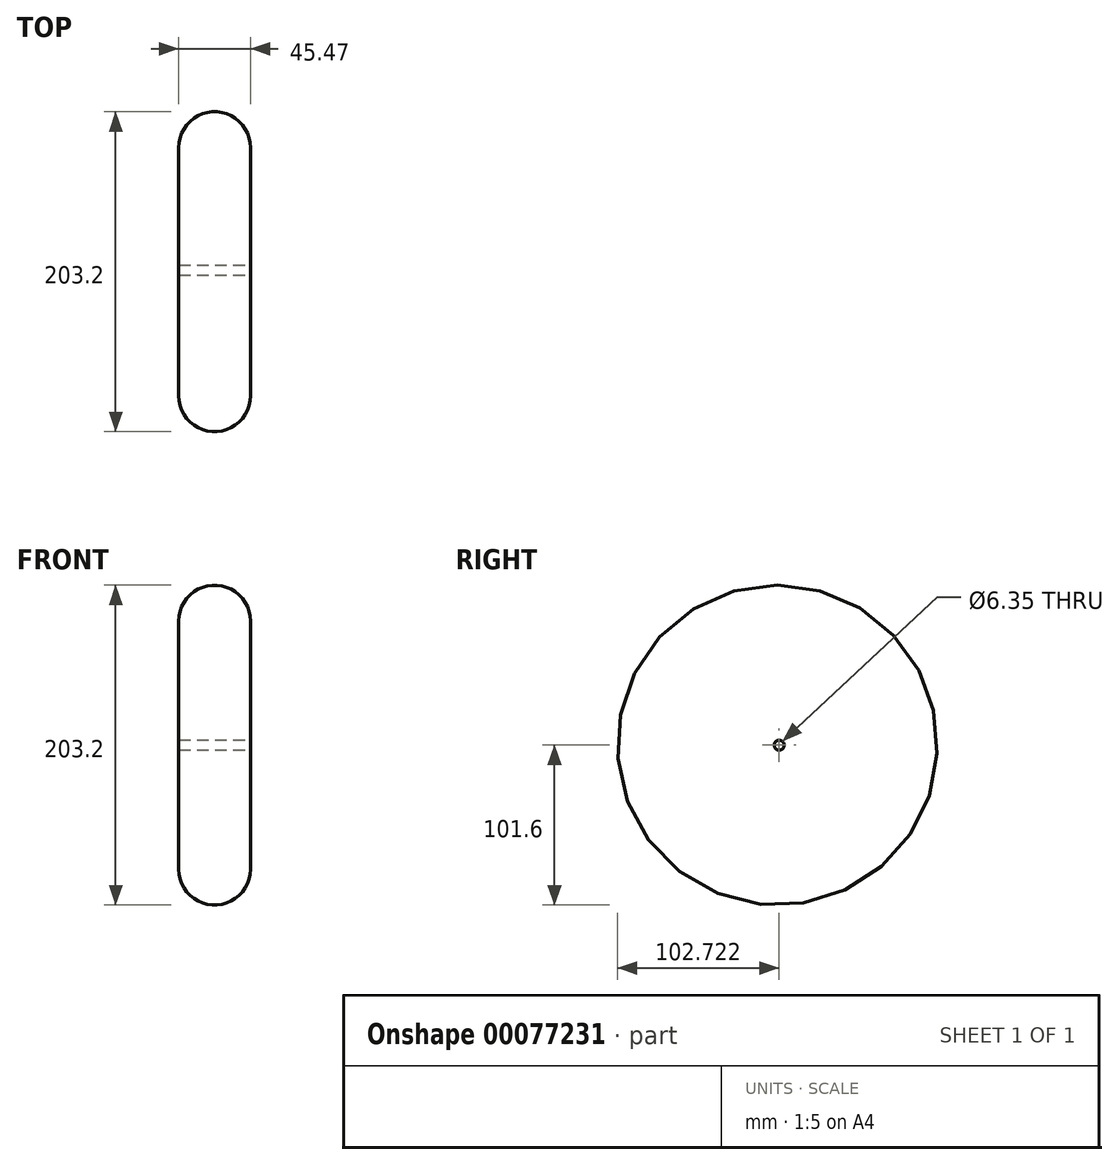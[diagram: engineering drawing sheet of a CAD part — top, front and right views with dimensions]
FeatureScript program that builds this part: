
annotation { "Feature Type Name" : "Feature", "Feature Type Description" : "" }
export const myFeature = defineFeature(function(context is Context, id is Id, definition is map)
    precondition{}
    {
        {
            var Q0;
            Q0=qCreatedBy(makeId("Front.planeOp"),FACE);
            var sketch = newSketch(context, id + "F0", { "sketchPlane" : qUnion([Q0])});
            skLineSegment(sketch, "E0", {"start": v(0, 78.87) * mm, "end": v(0, 0) * mm});
            skLineSegment(sketch, "E1", {"start": v(0, 0) * mm, "end": v(45.47, 0) * mm});
            skLineSegment(sketch, "E2", {"start": v(45.47, 0) * mm, "end": v(45.47, 78.87) * mm});
            skArc(sketch, "E3", {"start": v(45.47, 78.87) * mm, "mid": v(22.73, 101.6) * mm, "end": v(0, 78.87) * mm});
            skPoint(sketch, "E4", {"position": v(22.73, 101.6) * mm});
            skPoint(sketch, "E4.positionSnap0", {"position": v(22.73, 101.6) * mm});
            skSolve(sketch);
        }
        {
            var Q0;
            Q0=makeQuery(id+"F0.imprint","IMPRINT",FACE,{"disambiguationData":[TD([[makeQuery(id+"F0.imprint","IMPRINT",EDGE,{"derivedFrom":sQuery(id+"F0.wireOp",EDGE,"E0")}),1.0]])]});
            var Q1;
            Q1=sQuery(id+"F0.wireOp",EDGE,"E1");
            revolve(context, id + "F1", {"entities" : qUnion([Q0]), "axis" : qUnion([Q1]), "revolveType" : RevolveType.FULL});
        }
        {
            var Q0;
            Q0=makeQuery(id+"F1.opRevolve","SWEPT_FACE",FACE,{"disambiguationData":[OSD([sQuery(id+"F0.wireOp",EDGE,"E2")])]});
            var sketch = newSketch(context, id + "F2", { "sketchPlane" : qUnion([Q0])});
            skCircle(sketch, "E5", {"center": v(1.12, 0) * mm, "radius": 3.18 * mm});
            skSolve(sketch);
        }
        {
            var Q0;
            Q0 = qSketchRegion(id + "F2", true);
            extrude(context, id + "F3", {"entities" : qUnion([Q0]), "operationType" : NewBodyOperationType.REMOVE, "oppositeDirection" : true, "depth" : 50.8 * mm});
        }
    });
